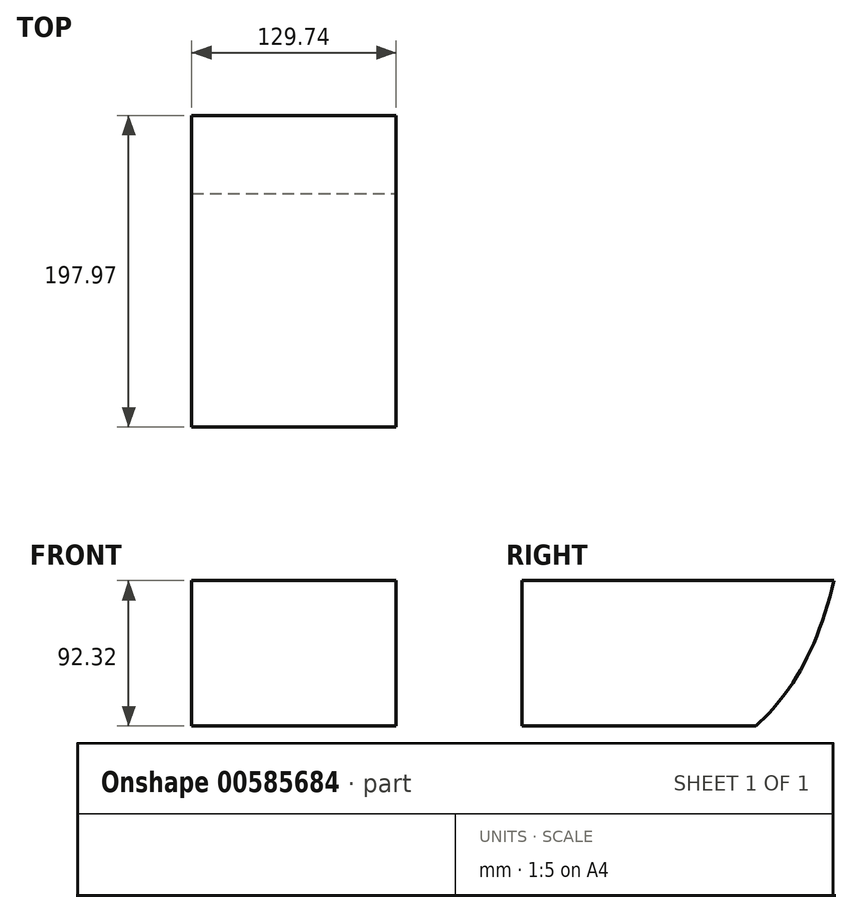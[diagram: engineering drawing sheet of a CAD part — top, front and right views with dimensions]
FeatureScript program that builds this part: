
annotation { "Feature Type Name" : "Feature", "Feature Type Description" : "" }
export const myFeature = defineFeature(function(context is Context, id is Id, definition is map)
    precondition{}
    {
        {
            var Q0;
            Q0=qCreatedBy(makeId("Right.planeOp"),FACE);
            var sketch = newSketch(context, id + "F0", { "sketchPlane" : qUnion([Q0])});
            skFitSpline(sketch, "E0", {"points": [v(127.04, -63.33) * mm, v(171.82, -19.03) * mm, v(202.6, 84.07) * mm], "startDerivative": vector(113.93, 84.9) * mm, "endDerivative": vector(4.57, 200.12) * mm});
            skSolve(sketch);
        }
        {
            var Q0;
            Q0=sQuery(id+"F0.wireOp",EDGE,"E0");
            extrude(context, id + "F1", {"bodyType" : ToolBodyType.SURFACE, "surfaceEntities" : qUnion([Q0]), "depth" : 100 * mm, "offsetDistance" : 25 * mm, "hasSecondDirection" : true, "secondDirectionOppositeDirection" : true, "secondDirectionDepth" : 100 * mm});
        }
        {
            var Q0;
            Q0=qCreatedBy(makeId("Front.planeOp"),FACE);
            var sketch = newSketch(context, id + "F2", { "sketchPlane" : qUnion([Q0])});
            skLineSegment(sketch, "E1.bottom", {"start": v(64.87, 46.16) * mm, "end": v(-64.87, 46.16) * mm});
            skLineSegment(sketch, "E1.top", {"start": v(64.87, -46.16) * mm, "end": v(-64.87, -46.16) * mm});
            skLineSegment(sketch, "E1.left", {"start": v(64.87, 46.16) * mm, "end": v(64.87, -46.16) * mm});
            skLineSegment(sketch, "E1.right", {"start": v(-64.87, 46.16) * mm, "end": v(-64.87, -46.16) * mm});
            skPoint(sketch, "E1.middle", {"position": v(0, 0) * mm});
            skSolve(sketch);
        }
        {
            var Q0;
            Q0=makeQuery(id+"F2.imprint","IMPRINT",FACE,{"disambiguationData":[TD([[makeQuery(id+"F2.imprint","IMPRINT",EDGE,{"derivedFrom":sQuery(id+"F2.wireOp",EDGE,"E1.bottom")}),1.0]])]});
            var Q1;
            Q1=makeQuery(id+"F1.opExtrude","SWEPT_FACE",FACE,{"disambiguationData":[OSD([sQuery(id+"F0.wireOp",EDGE,"E0")])]});
            extrude(context, id + "F3", {"entities" : qUnion([Q0]), "endBound" : BoundingType.UP_TO_SURFACE, "oppositeDirection" : true, "depth" : 122.39 * mm, "endBoundEntityFace" : qUnion([Q1]), "offsetDistance" : 25 * mm});
        }
    });
